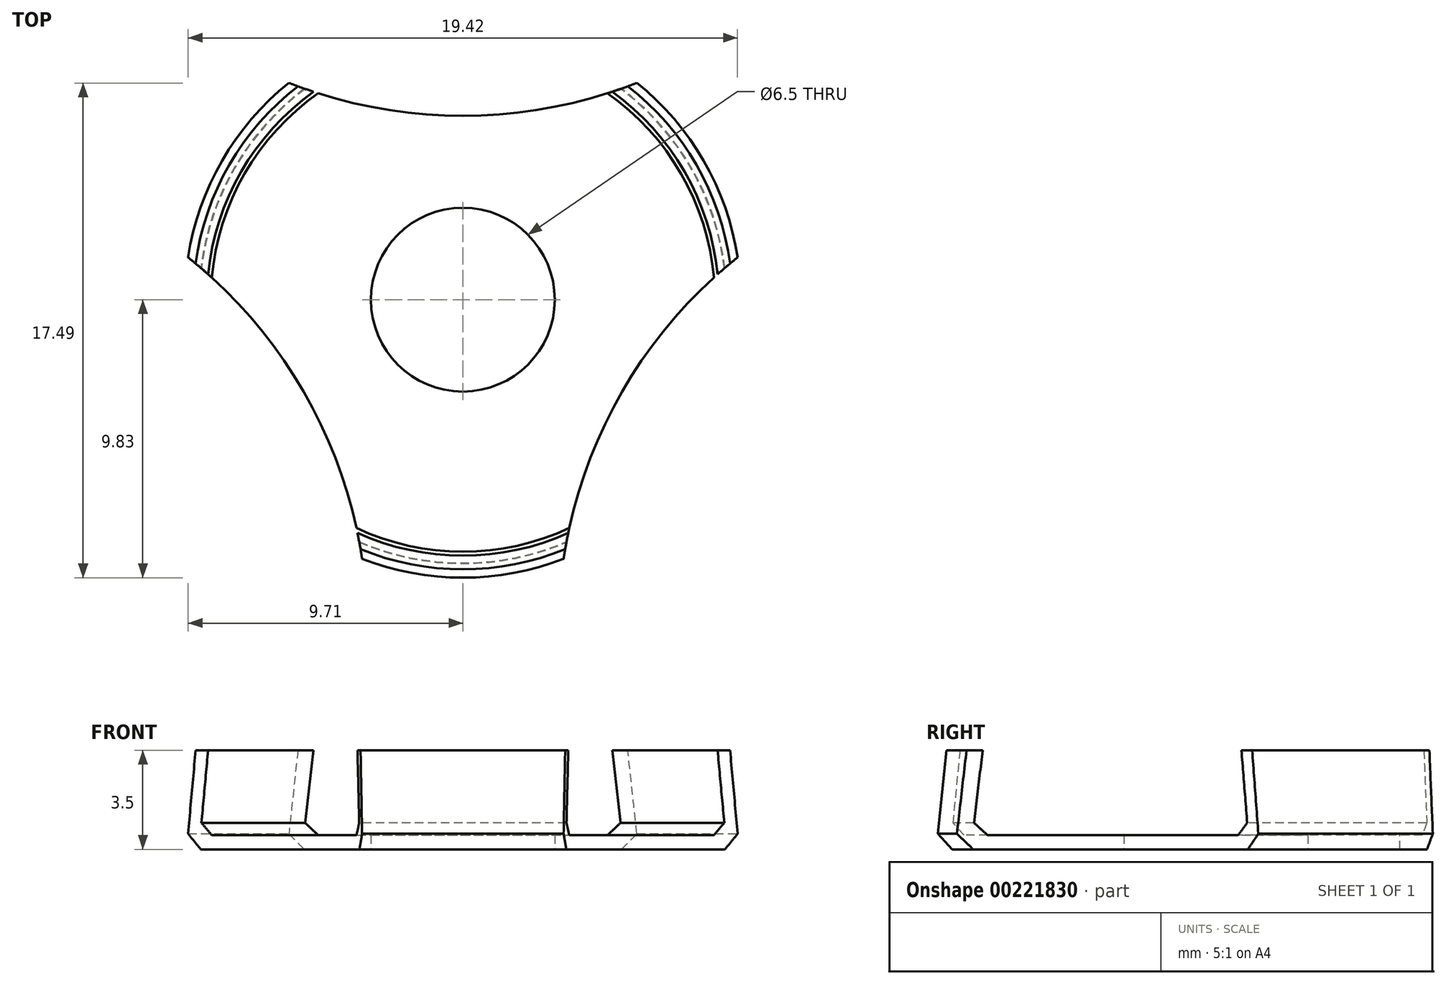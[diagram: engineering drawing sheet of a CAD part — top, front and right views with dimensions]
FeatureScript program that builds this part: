
annotation { "Feature Type Name" : "Feature", "Feature Type Description" : "" }
export const myFeature = defineFeature(function(context is Context, id is Id, definition is map)
    precondition{}
    {
        {
            var Q0;
            Q0=qCreatedBy(makeId("Front.planeOp"),FACE);
            var sketch = newSketch(context, id + "F0", { "sketchPlane" : qUnion([Q0])});
            skLineSegment(sketch, "E0", {"start": v(-9.88, -0.5) * mm, "end": v(-9.53, 3) * mm});
            skLineSegment(sketch, "E1.0", {"start": v(-9.53, 3) * mm, "end": v(-9.05, 3) * mm});
            skLineSegment(sketch, "E2.0", {"start": v(-9.88, -0.5) * mm, "end": v(-3.25, -0.5) * mm});
            skLineSegment(sketch, "E3.0", {"start": v(-9.35, 0) * mm, "end": v(-3.25, 0) * mm});
            skLineSegment(sketch, "E4", {"start": v(-9.05, 3) * mm, "end": v(-9.35, 0) * mm});
            skLineSegment(sketch, "E5", {"start": v(-3.25, 0) * mm, "end": v(-3.25, -0.5) * mm});
            skLineSegment(sketch, "E6", {"start": v(0, 0) * mm, "end": v(0, 3) * mm, "construction": true});
            skLineSegment(sketch, "E7.MirrorCS", {"start": v(3.25, 0) * mm, "end": v(3.25, -0.5) * mm, "construction": true});
            skLineSegment(sketch, "E8.MirrorCS", {"start": v(9.53, 3) * mm, "end": v(9.05, 3) * mm, "construction": true});
            skLineSegment(sketch, "E9.MirrorCS", {"start": v(9.05, 3) * mm, "end": v(9.35, 0) * mm, "construction": true});
            skLineSegment(sketch, "E10.MirrorCS", {"start": v(9.88, -0.5) * mm, "end": v(3.25, -0.5) * mm, "construction": true});
            skLineSegment(sketch, "E11.MirrorCS", {"start": v(9.88, -0.5) * mm, "end": v(9.53, 3) * mm, "construction": true});
            skLineSegment(sketch, "E12.MirrorCS", {"start": v(9.35, 0) * mm, "end": v(3.25, 0) * mm, "construction": true});
            skSolve(sketch);
        }
        {
            var Q0;
            Q0=qSketchRegion(id+"F0",true);
            var Q1;
            Q1=sQuery(id+"F0.wireOp",EDGE,"E6");
            revolve(context, id + "F1", {"entities" : qUnion([Q0]), "axis" : qUnion([Q1]), "revolveType" : RevolveType.FULL});
        }
        {
            var Q0;
            Q0=makeQuery(id+"FGJ8Jdsgf8nahhg_0.opExtrude","CAP_EDGE",EDGE,{"disambiguationData":[OSD([sQuery(id+"FfD0BnyzNT35BCW_0.wireOp",EDGE,"XXezrp6G-6KFv-04YQ-ZBWx-PVepfeV2B4WU")])],"isStart":false});
            var Q1;
            Q1=makeQuery(id+"F1.opRevolve","SWEPT_EDGE",EDGE,{"disambiguationData":[OSD([sQuery(id+"F0.wireOp",EDGE,"E0"),sQuery(id+"F0.wireOp",EDGE,"E2.0")])]});
            chamfer(context, id + "F2", {"entities" : qUnion([Q0, Q1]), "width" : .5 * mm, "tangentPropagation" : true});
        }
        {
            var Q0;
            Q0=makeQuery(id+"FSM4ZXUINE7IlSd_1.opExtrude","CAP_EDGE",EDGE,{"disambiguationData":[OSD([sQuery(id+"FfD0BnyzNT35BCW_0.wireOp",EDGE,"7iooxUre-ZOTs-RTEa-hMcE-vPOAERNByD5Q")])],"isStart":true});
            var Q1;
            Q1=makeQuery(id+"F1.opRevolve","SWEPT_EDGE",EDGE,{"disambiguationData":[OSD([sQuery(id+"F0.wireOp",EDGE,"E3.0"),sQuery(id+"F0.wireOp",EDGE,"E4")])]});
            chamfer(context, id + "F3", {"entities" : qUnion([Q0, Q1]), "width" : .4 * mm, "tangentPropagation" : true});
        }
        {
            var Q0;
            Q0=makeQuery(id+"F1.opRevolve","SWEPT_FACE",FACE,{"disambiguationData":[OSD([sQuery(id+"F0.wireOp",EDGE,"E2.0")])]});
            var sketch = newSketch(context, id + "F4", { "sketchPlane" : qUnion([Q0])});
            skPoint(sketch, "E13.center", {"position": v(0, 0) * mm});
            skCircle(sketch, "E14", {"center": v(0, 0) * mm, "radius": 6.5 * mm, "construction": true});
            skLineSegment(sketch, "E15", {"start": v(0, 0) * mm, "end": v(0, -23.33) * mm, "construction": true});
            skLineSegment(sketch, "E16.1.0", {"start": v(0, 0) * mm, "end": v(20.2, 11.66) * mm, "construction": true});
            skLineSegment(sketch, "E16.2.0", {"start": v(0, 0) * mm, "end": v(-20.2, 11.66) * mm, "construction": true});
            skCircle(sketch, "E17", {"center": v(0, -23.33) * mm, "radius": 16.83 * mm});
            skCircle(sketch, "E18.1.0", {"center": v(20.2, 11.66) * mm, "radius": 16.83 * mm});
            skCircle(sketch, "E18.2.0", {"center": v(-20.2, 11.66) * mm, "radius": 16.83 * mm});
            skSolve(sketch);
        }
        {
            var Q0;
            Q0=makeQuery(id+"F4.imprint","IMPRINT",FACE,{"disambiguationData":[TD([[makeQuery(id+"F4.imprint","IMPRINT",EDGE,{"derivedFrom":sQuery(id+"F4.wireOp",EDGE,"E17")}),1.0]])]});
            var Q1;
            Q1=makeQuery(id+"F4.imprint","IMPRINT",FACE,{"disambiguationData":[TD([[makeQuery(id+"F4.imprint","IMPRINT",EDGE,{"derivedFrom":sQuery(id+"F4.wireOp",EDGE,"E18.1.0")}),1.0]])]});
            var Q2;
            Q2=makeQuery(id+"F4.imprint","IMPRINT",FACE,{"disambiguationData":[TD([[makeQuery(id+"F4.imprint","IMPRINT",EDGE,{"derivedFrom":sQuery(id+"F4.wireOp",EDGE,"E18.2.0")}),1.0]])]});
            extrude(context, id + "F5", {"entities" : qUnion([Q0, Q1, Q2]), "operationType" : NewBodyOperationType.REMOVE, "depth" : 25 * mm, "symmetric" : true});
        }
    });
